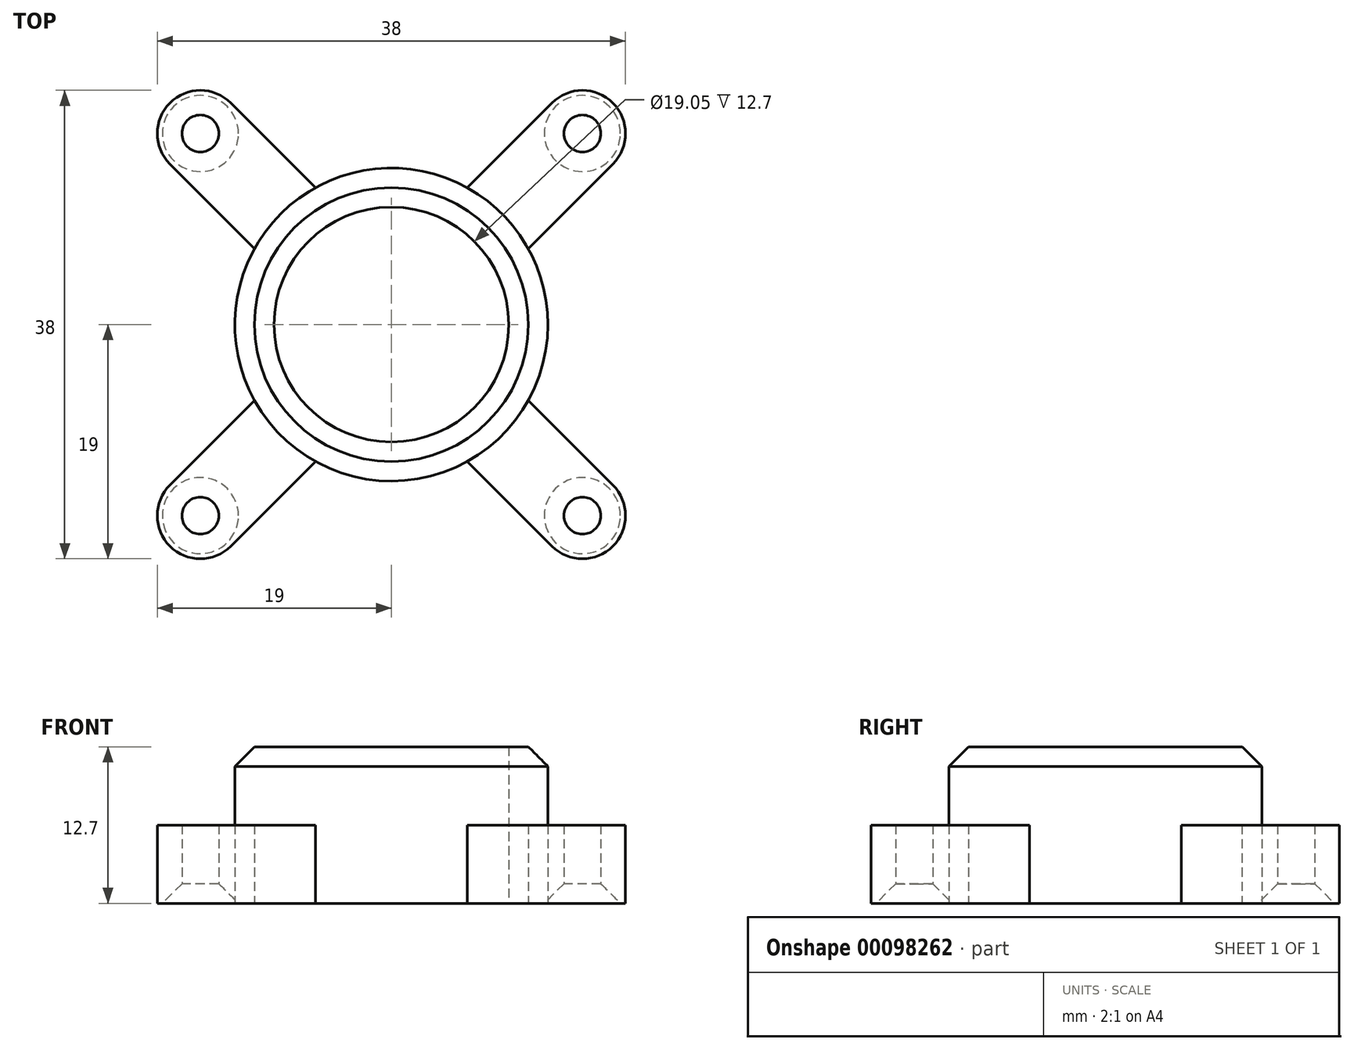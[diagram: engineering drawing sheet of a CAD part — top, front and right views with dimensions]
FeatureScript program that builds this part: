
annotation { "Feature Type Name" : "Feature", "Feature Type Description" : "" }
export const myFeature = defineFeature(function(context is Context, id is Id, definition is map)
    precondition{}
    {
        {
            var Q0;
            Q0=qCreatedBy(makeId("Top.planeOp"),FACE);
            var sketch = newSketch(context, id + "F0", { "sketchPlane" : qUnion([Q0])});
            skArc(sketch, "E0", {"start": v(-11.1, 6.16) * mm, "mid": v(-12.7, 0) * mm, "end": v(-11.1, -6.16) * mm});
            skLineSegment(sketch, "E1", {"start": v(0, 0) * mm, "end": v(0, 15.5) * mm, "construction": true});
            skLineSegment(sketch, "E2", {"start": v(0, 15.5) * mm, "end": v(15.5, 15.5) * mm, "construction": true});
            skCircle(sketch, "E3", {"center": v(15.5, 15.5) * mm, "radius": 1.5 * mm});
            skCircle(sketch, "E4.1.0", {"center": v(-15.5, 15.5) * mm, "radius": 1.5 * mm});
            skCircle(sketch, "E4.2.0", {"center": v(-15.5, -15.5) * mm, "radius": 1.5 * mm});
            skCircle(sketch, "E4.3.0", {"center": v(15.5, -15.5) * mm, "radius": 1.5 * mm});
            skArc(sketch, "E5.0", {"start": v(17.97, 13.03) * mm, "mid": v(17.97, 17.97) * mm, "end": v(13.03, 17.97) * mm});
            skLineSegment(sketch, "E6", {"start": v(15.5, 15.5) * mm, "end": v(0, 0) * mm, "construction": true});
            skLineSegment(sketch, "E7.0", {"start": v(13.03, 17.97) * mm, "end": v(6.16, 11.1) * mm});
            skLineSegment(sketch, "E8.MirrorCS", {"start": v(17.97, 13.03) * mm, "end": v(11.1, 6.16) * mm});
            skPoint(sketch, "E9.orphan", {"position": v(2.47, -2.47) * mm});
            skPoint(sketch, "E10.trimOffspring.end.orphan", {"position": v(-2.47, 2.47) * mm});
            skCircle(sketch, "E11.0", {"center": v(0, 0) * mm, "radius": 9.53 * mm});
            skArc(sketch, "E12.1.0", {"start": v(-13.03, 17.97) * mm, "mid": v(-17.97, 17.97) * mm, "end": v(-17.97, 13.03) * mm});
            skLineSegment(sketch, "E12.1.1", {"start": v(-13.03, 17.97) * mm, "end": v(-6.16, 11.1) * mm});
            skLineSegment(sketch, "E12.1.2", {"start": v(-17.97, 13.03) * mm, "end": v(-11.1, 6.16) * mm});
            skArc(sketch, "E12.2.0", {"start": v(-17.97, -13.03) * mm, "mid": v(-17.97, -17.97) * mm, "end": v(-13.03, -17.97) * mm});
            skLineSegment(sketch, "E12.2.1", {"start": v(-17.97, -13.03) * mm, "end": v(-11.1, -6.16) * mm});
            skLineSegment(sketch, "E12.2.2", {"start": v(-13.03, -17.97) * mm, "end": v(-6.16, -11.1) * mm});
            skArc(sketch, "E12.3.0", {"start": v(13.03, -17.97) * mm, "mid": v(17.97, -17.97) * mm, "end": v(17.97, -13.03) * mm});
            skLineSegment(sketch, "E12.3.1", {"start": v(13.03, -17.97) * mm, "end": v(6.16, -11.1) * mm});
            skLineSegment(sketch, "E12.3.2", {"start": v(17.97, -13.03) * mm, "end": v(11.1, -6.16) * mm});
            skArc(sketch, "E13.trimOffspring", {"start": v(-6.16, -11.1) * mm, "mid": v(0, -12.7) * mm, "end": v(6.16, -11.1) * mm});
            skArc(sketch, "E14.trimOffspring", {"start": v(11.1, -6.16) * mm, "mid": v(12.7, 0) * mm, "end": v(11.1, 6.16) * mm});
            skArc(sketch, "E15.trimOffspring", {"start": v(6.16, 11.1) * mm, "mid": v(0, 12.7) * mm, "end": v(-6.16, 11.1) * mm});
            skSolve(sketch);
        }
        {
            var Q0;
            Q0 = qSketchRegion(id + "F0", true);
            extrude(context, id + "F1", {"entities" : qUnion([Q0]), "depth" : 6.35 * mm});
        }
        {
            var Q0;
            Q0=makeQuery(id+"F1.opExtrude","CAP_EDGE",EDGE,{"disambiguationData":[OSD([sQuery(id+"F0.wireOp",EDGE,"E4.2.0")])],"isStart":true});
            var Q1;
            Q1=makeQuery(id+"F1.opExtrude","CAP_EDGE",EDGE,{"disambiguationData":[OSD([sQuery(id+"F0.wireOp",EDGE,"E4.3.0")])],"isStart":true});
            var Q2;
            Q2=makeQuery(id+"F1.opExtrude","CAP_EDGE",EDGE,{"disambiguationData":[OSD([sQuery(id+"F0.wireOp",EDGE,"E3")])],"isStart":true});
            var Q3;
            Q3=makeQuery(id+"F1.opExtrude","CAP_EDGE",EDGE,{"disambiguationData":[OSD([sQuery(id+"F0.wireOp",EDGE,"E4.1.0")])],"isStart":true});
            chamfer(context, id + "F2", {"entities" : qUnion([Q0, Q1, Q2, Q3]), "width" : 1.59 * mm, "tangentPropagation" : true});
        }
        {
            var Q0;
            Q0=makeQuery(id+"F1.opExtrude","CAP_FACE",FACE,{"disambiguationData":[OSD([sQuery(id+"F0.wireOp",EDGE,"E0"),sQuery(id+"F0.wireOp",EDGE,"E3"),sQuery(id+"F0.wireOp",EDGE,"E4.1.0"),sQuery(id+"F0.wireOp",EDGE,"E4.2.0"),sQuery(id+"F0.wireOp",EDGE,"E4.3.0"),sQuery(id+"F0.wireOp",EDGE,"E5.0"),sQuery(id+"F0.wireOp",EDGE,"E7.0"),sQuery(id+"F0.wireOp",EDGE,"E8.MirrorCS"),sQuery(id+"F0.wireOp",EDGE,"E11.0"),sQuery(id+"F0.wireOp",EDGE,"E12.1.0"),sQuery(id+"F0.wireOp",EDGE,"E12.1.1"),sQuery(id+"F0.wireOp",EDGE,"E12.1.2"),sQuery(id+"F0.wireOp",EDGE,"E12.2.0"),sQuery(id+"F0.wireOp",EDGE,"E12.2.1"),sQuery(id+"F0.wireOp",EDGE,"E12.2.2"),sQuery(id+"F0.wireOp",EDGE,"E12.3.0"),sQuery(id+"F0.wireOp",EDGE,"E12.3.1"),sQuery(id+"F0.wireOp",EDGE,"E12.3.2"),sQuery(id+"F0.wireOp",EDGE,"E13.trimOffspring"),sQuery(id+"F0.wireOp",EDGE,"E14.trimOffspring"),sQuery(id+"F0.wireOp",EDGE,"E15.trimOffspring")])],"isStart":false});
            var sketch = newSketch(context, id + "F3", { "sketchPlane" : qUnion([Q0])});
            skCircle(sketch, "E16", {"center": v(0, 0) * mm, "radius": 9.53 * mm});
            skCircle(sketch, "E17", {"center": v(0, 0) * mm, "radius": 12.7 * mm});
            skSolve(sketch);
        }
        {
            var Q0;
            Q0 = qSketchRegion(id + "F3", true);
            extrude(context, id + "F4", {"entities" : qUnion([Q0]), "operationType" : NewBodyOperationType.ADD, "depth" : 6.35 * mm});
        }
        {
            var Q0;
            Q0=makeQuery(id+"F4.opExtrude","CAP_EDGE",EDGE,{"disambiguationData":[OSD([sQuery(id+"F3.wireOp",EDGE,"E17")])],"isStart":false});
            chamfer(context, id + "F5", {"entities" : qUnion([Q0]), "width" : 1.59 * mm, "tangentPropagation" : true});
        }
    });
